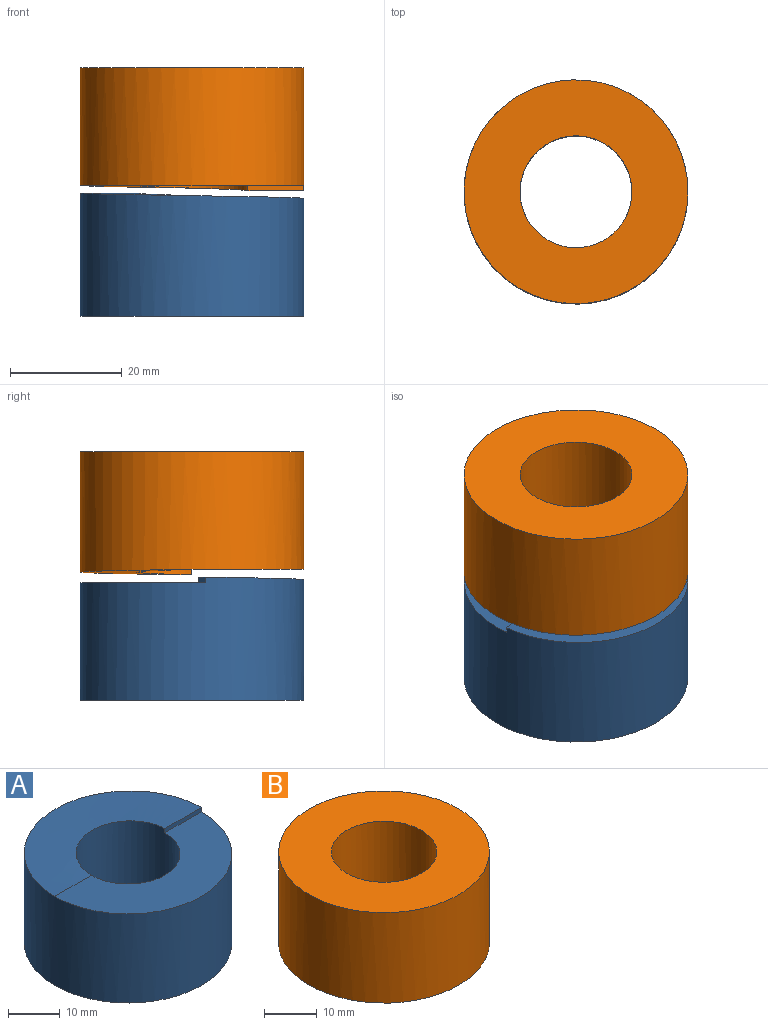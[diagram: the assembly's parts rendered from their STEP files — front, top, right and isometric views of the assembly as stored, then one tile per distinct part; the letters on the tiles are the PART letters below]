
ASSEMBLY  parts=2 mates=1
PART A: 6 faces, bbox 40x43.1x22 mm
  f0: plane 40x20mm, normal (0,0,1), area 471.2mm2, adj f1,f2,f4,f5
  f1: cylinder r=10mm len=22mm, axis (0,0,1), area 1335.2mm2, adj f0,f3,f4,f5
  f2: cylinder r=20mm len=40mm, axis (0,0,1), area 2670.4mm2, adj f0,f3,f4,f5
  f3: plane 40x40mm, normal (0,0,-1), area 942.5mm2, adj f1,f2
  f4: plane 10x1mm, normal (0,-1,0), area 10mm2, adj f0,f1,f2,f5
  f5: bspline ~40.41x40mm, area 471.2mm2, adj f0,f1,f2,f4
PART B: 6 faces, bbox 40x43.1x22 mm
  f0: plane 40x20mm, normal (0,0,-1), area 471.2mm2, adj f1,f2,f4,f5
  f1: cylinder r=10mm len=22mm, axis (0,0,-1), area 1335.2mm2, adj f0,f3,f4,f5
  f2: cylinder r=20mm len=40mm, axis (0,0,-1), area 2670.4mm2, adj f0,f3,f4,f5
  f3: plane 40x40mm, normal (0,0,1), area 942.5mm2, adj f1,f2
  f4: plane 10x1mm, normal (0,-1,0), area 10mm2, adj f0,f1,f2,f5
  f5: bspline ~40.41x40mm, area 471.2mm2, adj f0,f1,f2,f4
PLACE A rot(axis=(0,0,-1),173.3deg) t=(0,0,17.61)mm
PLACE B at identity fixed
MATE cylindrical B.f2 <-> A.f1  axis (0,0,1) through (0,0,41)mm
